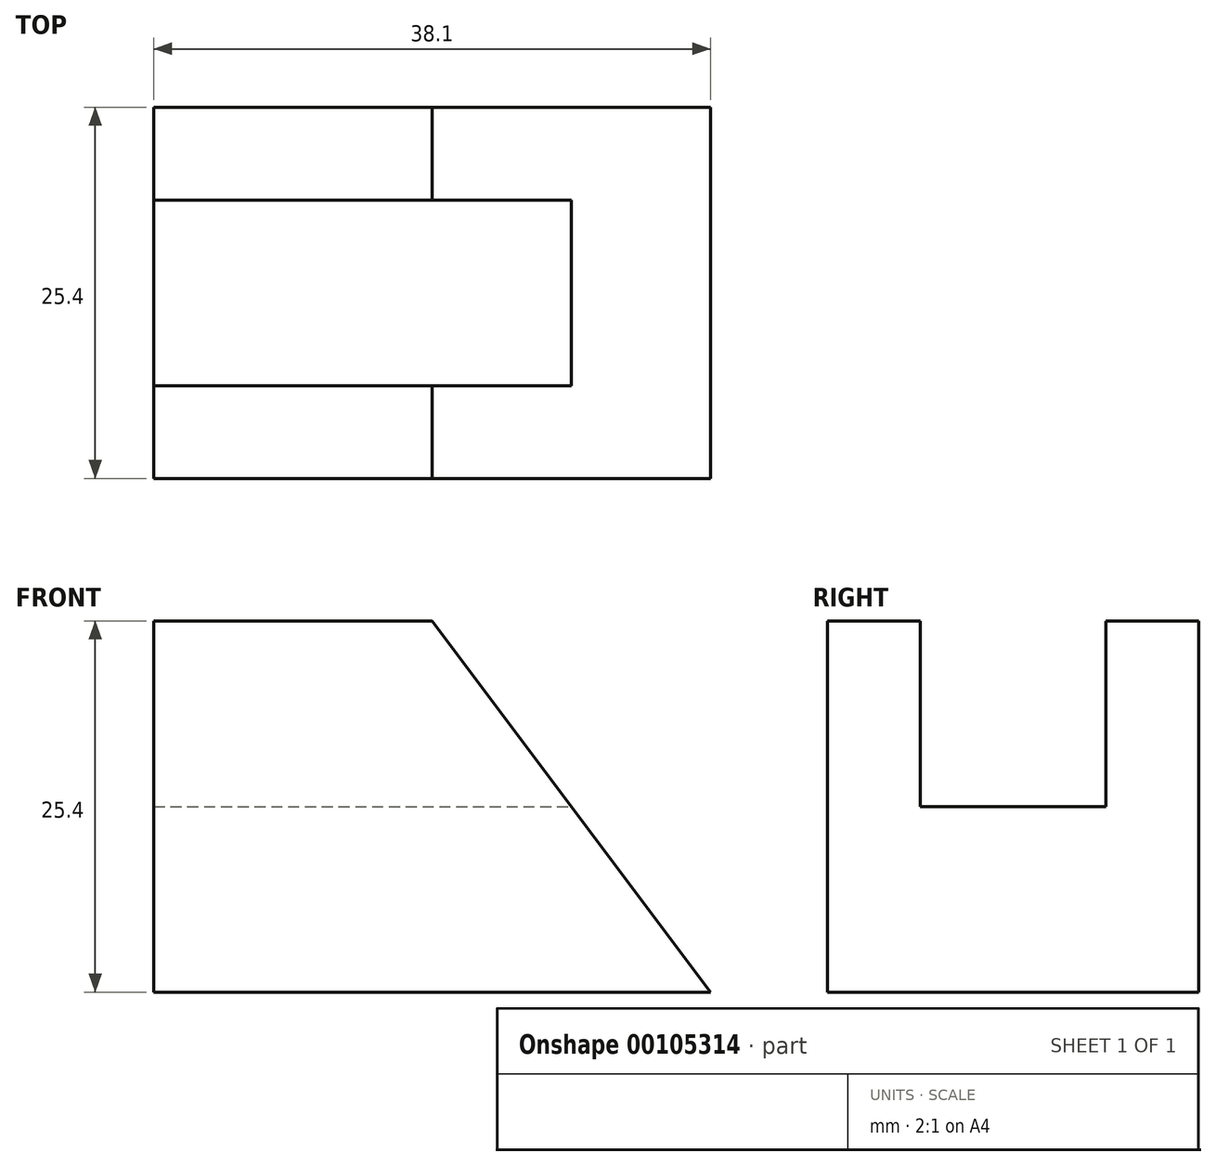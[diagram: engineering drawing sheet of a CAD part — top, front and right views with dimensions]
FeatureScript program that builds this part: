
annotation { "Feature Type Name" : "Feature", "Feature Type Description" : "" }
export const myFeature = defineFeature(function(context is Context, id is Id, definition is map)
    precondition{}
    {
        {
            var Q0;
            Q0=qCreatedBy(makeId("Front.planeOp"),FACE);
            var sketch = newSketch(context, id + "F0", { "sketchPlane" : qUnion([Q0])});
            skLineSegment(sketch, "E0", {"start": v(0, 0) * mm, "end": v(0, 25.4) * mm});
            skLineSegment(sketch, "E1", {"start": v(0, 25.4) * mm, "end": v(19.05, 25.4) * mm});
            skLineSegment(sketch, "E2", {"start": v(19.05, 25.4) * mm, "end": v(38.1, 0) * mm});
            skLineSegment(sketch, "E3", {"start": v(38.1, 0) * mm, "end": v(0, 0) * mm});
            skLineSegment(sketch, "E4", {"start": v(28.57, 12.7) * mm, "end": v(0, 12.7) * mm});
            skSolve(sketch);
        }
        {
            var Q0;
            Q0 = qSketchRegion(id + "F0", true);
            extrude(context, id + "F1", {"entities" : qUnion([Q0]), "endBound" : BoundingType.SYMMETRIC, "depth" : 25.4 * mm});
        }
        {
            var Q0;
            Q0=qCreatedBy(makeId("Front.planeOp"),FACE);
            var sketch = newSketch(context, id + "F2", { "sketchPlane" : qUnion([Q0])});
            skLineSegment(sketch, "E5", {"start": v(0, 12.7) * mm, "end": v(28.57, 12.7) * mm});
            skLineSegment(sketch, "E6", {"start": v(28.58, 12.7) * mm, "end": v(19.05, 25.4) * mm});
            skLineSegment(sketch, "E7", {"start": v(19.05, 25.4) * mm, "end": v(0, 25.4) * mm});
            skLineSegment(sketch, "E8", {"start": v(0, 25.4) * mm, "end": v(0, 12.7) * mm});
            skSolve(sketch);
        }
        {
            var Q0;
            Q0 = qSketchRegion(id + "F2", true);
            extrude(context, id + "F3", {"entities" : qUnion([Q0]), "operationType" : NewBodyOperationType.REMOVE, "endBound" : BoundingType.SYMMETRIC, "depth" : 12.7 * mm});
        }
    });
